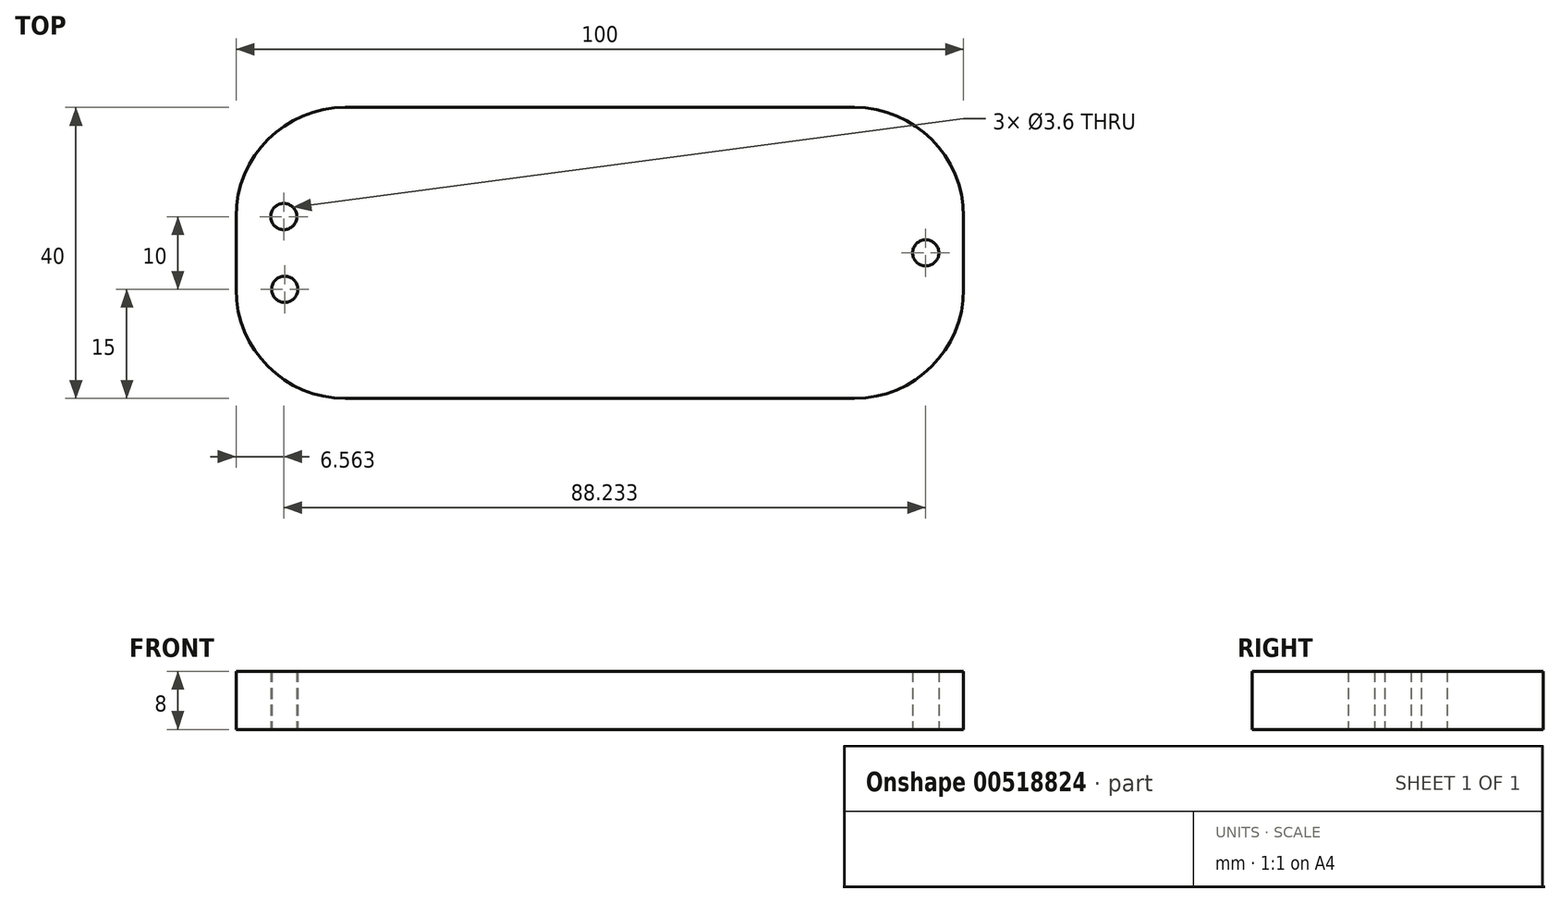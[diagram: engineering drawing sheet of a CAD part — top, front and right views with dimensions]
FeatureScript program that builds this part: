
annotation { "Feature Type Name" : "Feature", "Feature Type Description" : "" }
export const myFeature = defineFeature(function(context is Context, id is Id, definition is map)
    precondition{}
    {
        {
            var Q0;
            Q0=qCreatedBy(makeId("Top.planeOp"),FACE);
            var sketch = newSketch(context, id + "F0", { "sketchPlane" : qUnion([Q0])});
            skLineSegment(sketch, "E0.bottom", {"start": v(35, 20) * mm, "end": v(-35, 20) * mm});
            skLineSegment(sketch, "E0.top", {"start": v(35, -20) * mm, "end": v(-35, -20) * mm});
            skLineSegment(sketch, "E0.left", {"start": v(50, 5) * mm, "end": v(50, -5) * mm});
            skLineSegment(sketch, "E0.right", {"start": v(-50, 5) * mm, "end": v(-50, -5) * mm});
            skPoint(sketch, "E0.middle", {"position": v(0, 0) * mm});
            skPoint(sketch, "E1.visualSharp", {"position": v(-50, -20) * mm});
            skArc(sketch, "E1.filletArc", {"start": v(-50, -5) * mm, "mid": v(-45.6, -15.6) * mm, "end": v(-35, -20) * mm});
            skPoint(sketch, "E2.visualSharp", {"position": v(-50, 20) * mm});
            skArc(sketch, "E2.filletArc", {"start": v(-35, 20) * mm, "mid": v(-45.6, 15.6) * mm, "end": v(-50, 5) * mm});
            skPoint(sketch, "E3.visualSharp", {"position": v(50, -20) * mm});
            skArc(sketch, "E3.filletArc", {"start": v(35, -20) * mm, "mid": v(45.6, -15.6) * mm, "end": v(50, -5) * mm});
            skPoint(sketch, "E4.visualSharp", {"position": v(50, 20) * mm});
            skArc(sketch, "E4.filletArc", {"start": v(50, 5) * mm, "mid": v(45.6, 15.6) * mm, "end": v(35, 20) * mm});
            skSolve(sketch);
        }
        {
            var Q0;
            Q0 = qSketchRegion(id + "F0", true);
            extrude(context, id + "F1", {"entities" : qUnion([Q0]), "endBound" : BoundingType.SYMMETRIC, "depth" : 8 * mm, "offsetDistance" : 25 * mm});
        }
        {
            var Q0;
            Q0=makeQuery(id+"F1.opExtrude","CAP_FACE",FACE,{"disambiguationData":[OSD([sQuery(id+"F0.wireOp",EDGE,"E0.bottom"),sQuery(id+"F0.wireOp",EDGE,"E0.top"),sQuery(id+"F0.wireOp",EDGE,"E0.left"),sQuery(id+"F0.wireOp",EDGE,"E0.right"),sQuery(id+"F0.wireOp",EDGE,"E1.filletArc"),sQuery(id+"F0.wireOp",EDGE,"E2.filletArc"),sQuery(id+"F0.wireOp",EDGE,"E3.filletArc"),sQuery(id+"F0.wireOp",EDGE,"E4.filletArc")])],"isStart":true});
            var sketch = newSketch(context, id + "F2", { "sketchPlane" : qUnion([Q0])});
            skCircle(sketch, "E5", {"center": v(-43.31, 5) * mm, "radius": 1.8 * mm});
            skCircle(sketch, "E6", {"center": v(-43.44, -5) * mm, "radius": 1.8 * mm});
            skSolve(sketch);
        }
        {
            var Q0;
            Q0=makeQuery(id+"F2.imprint","IMPRINT",FACE,{"disambiguationData":[TD([[makeQuery(id+"F2.imprint","IMPRINT",EDGE,{"derivedFrom":sQuery(id+"F2.wireOp",EDGE,"E5")}),-1.0]])]});
            var sketch = newSketch(context, id + "F3", { "sketchPlane" : qUnion([Q0])});
            skCircle(sketch, "E7", {"center": v(44.8, 0) * mm, "radius": 1.8 * mm});
            skSolve(sketch);
        }
        {
            var Q0;
            Q0 = qSketchRegion(id + "F2", true);
            extrude(context, id + "F4", {"entities" : qUnion([Q0]), "operationType" : NewBodyOperationType.REMOVE, "oppositeDirection" : true, "depth" : 8 * mm, "offsetDistance" : 25 * mm});
        }
        {
            var Q0;
            Q0 = qSketchRegion(id + "F3", true);
            extrude(context, id + "F5", {"entities" : qUnion([Q0]), "operationType" : NewBodyOperationType.REMOVE, "oppositeDirection" : true, "depth" : 8 * mm, "offsetDistance" : 25 * mm});
        }
    });
